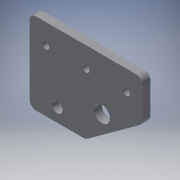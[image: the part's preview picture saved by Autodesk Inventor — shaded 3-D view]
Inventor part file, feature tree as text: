
AUTODESK INVENTOR PART (.ipt)
format: ipt  version: 2017 (Build 210142000, 142)  size: 272,384 bytes
history: native  units: mm
features: sketch x4, extrude x3, hole x1, projected_geometry x1
ambient origin geometry x8: Origin, YZ Plane, XZ Plane, XY Plane, X Axis, Y Axis, Z Axis, Center Point
bodies: Solid1 (feature_tree)
feature tree (9):
  extrude  "Extrusion1"  Depth=10.0mm TaperAngle=0.0deg
  hole  "Hole1"  [1 undecoded]
  extrude  "Extrusion2"  [1 undecoded]
  extrude  "Extrusion3"  [1 undecoded]
  sketch  "Sketch1"  dims[d0=6.0mm d1=0.0mm]
  sketch  "Sketch2"  dims[d2=5.2mm d3=6.0mm d4=4.0mm d5=2.0mm d6=90.0deg d7=8.0mm d8=20.594885mm d9=10.0mm d10=0.0mm]
  projected_geometry  "Projected Loop1"
  sketch  "Sketch3"  dims[d11=12.0mm d12=10.0mm d13=0.0mm]
  sketch  "Sketch5"
note: 3 required parameter values undecoded (feature->parameter linkage not recoverable at this tier; creation-order binding heuristic only, values carry confidence <= 0.55)
